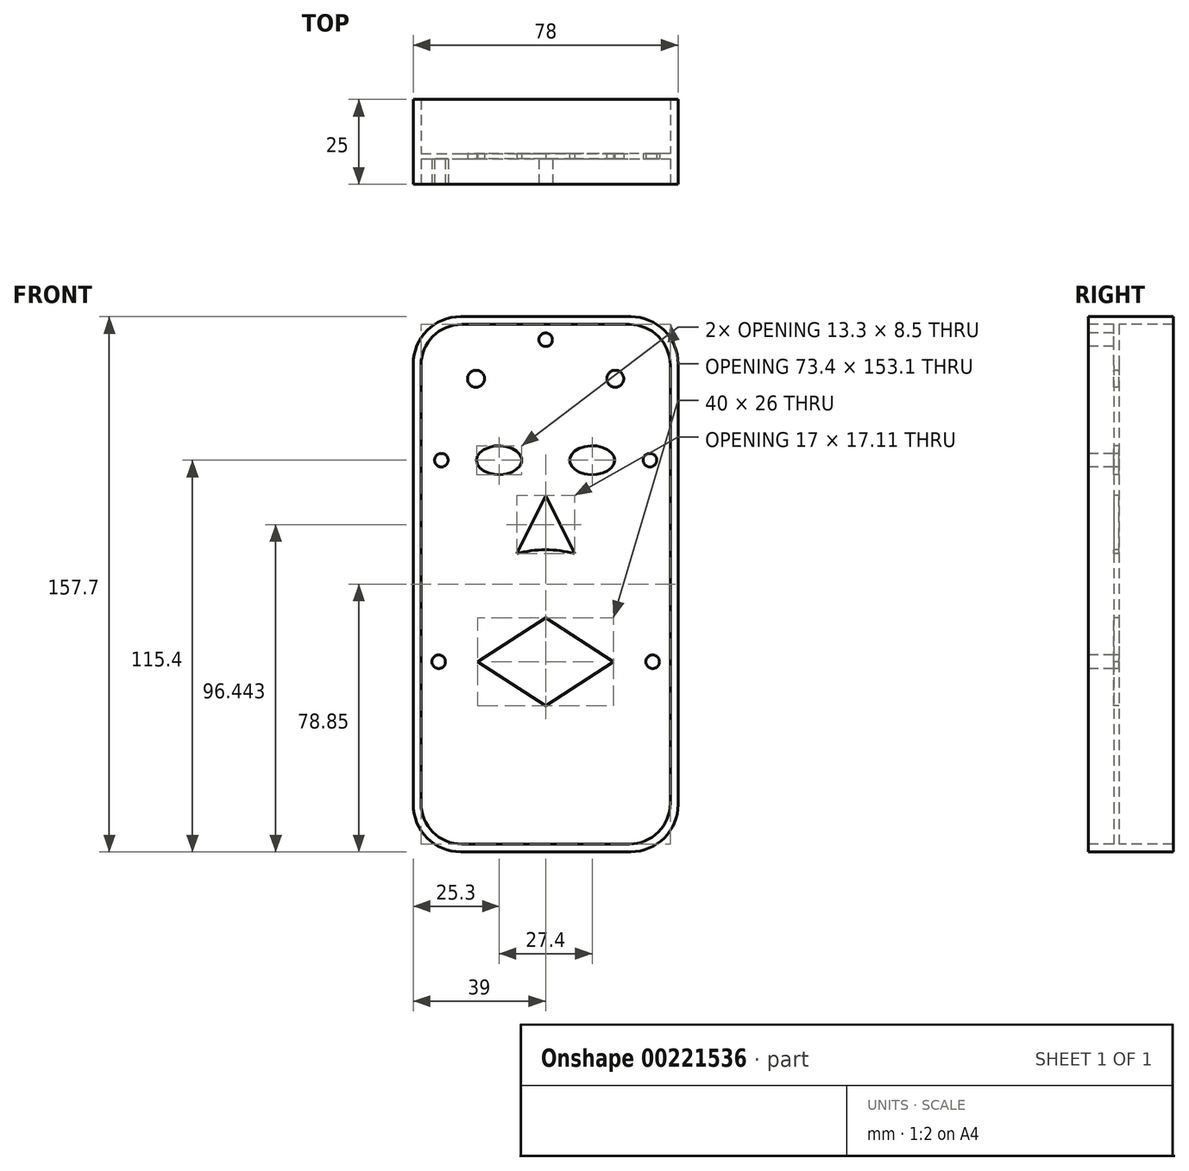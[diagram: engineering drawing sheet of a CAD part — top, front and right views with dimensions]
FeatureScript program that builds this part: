
annotation { "Feature Type Name" : "Feature", "Feature Type Description" : "" }
export const myFeature = defineFeature(function(context is Context, id is Id, definition is map)
    precondition{}
    {
        {
            var Q0;
            Q0=qCreatedBy(makeId("Front.planeOp"),FACE);
            var sketch = newSketch(context, id + "F0", { "sketchPlane" : qUnion([Q0])});
            skLineSegment(sketch, "E0.bottom", {"start": v(-39, 78.85) * mm, "end": v(39, 78.85) * mm});
            skLineSegment(sketch, "E0.top", {"start": v(-39, -78.85) * mm, "end": v(39, -78.85) * mm});
            skLineSegment(sketch, "E0.left", {"start": v(-39, 78.85) * mm, "end": v(-39, -78.85) * mm});
            skLineSegment(sketch, "E0.right", {"start": v(39, 78.85) * mm, "end": v(39, -78.85) * mm});
            skPoint(sketch, "E0.middle", {"position": v(0, 0) * mm});
            skLineSegment(sketch, "E1", {"start": v(-39, -22.85) * mm, "end": v(39, -22.85) * mm, "construction": true});
            skLineSegment(sketch, "E2", {"start": v(0, -9.85) * mm, "end": v(-20, -22.85) * mm});
            skPoint(sketch, "E2.startSnap0", {"position": v(0, -22.85) * mm});
            skLineSegment(sketch, "E3", {"start": v(-20, -22.85) * mm, "end": v(0, -35.85) * mm});
            skLineSegment(sketch, "E4.MirrorCS", {"start": v(0, -9.85) * mm, "end": v(20, -22.85) * mm});
            skLineSegment(sketch, "E5.MirrorCS", {"start": v(20, -22.85) * mm, "end": v(0, -35.85) * mm});
            skLineSegment(sketch, "E6.0", {"start": v(-36.7, 76.55) * mm, "end": v(-36.7, -76.55) * mm});
            skLineSegment(sketch, "E6.1", {"start": v(-36.7, 76.55) * mm, "end": v(36.7, 76.55) * mm});
            skLineSegment(sketch, "E6.2", {"start": v(36.7, 76.55) * mm, "end": v(36.7, -76.55) * mm});
            skLineSegment(sketch, "E6.3", {"start": v(-36.7, -76.55) * mm, "end": v(36.7, -76.55) * mm});
            skCircle(sketch, "E7", {"center": v(-31.5, -22.85) * mm, "radius": 2 * mm});
            skCircle(sketch, "E8.MirrorC", {"center": v(31.5, -22.85) * mm, "radius": 2 * mm});
            skArc(sketch, "E9", {"start": v(0, 10.15) * mm, "mid": v(-4.29, 9.87) * mm, "end": v(-8.5, 9.04) * mm});
            skLineSegment(sketch, "E10", {"start": v(-8.5, 9.04) * mm, "end": v(0, 26.15) * mm});
            skCircle(sketch, "E11", {"center": v(-3.04, 12.52) * mm, "radius": 2.5 * mm});
            skLineSegment(sketch, "E12.MirrorCS", {"start": v(8.5, 9.04) * mm, "end": v(0, 26.15) * mm});
            skCircle(sketch, "E13.MirrorC", {"center": v(3.04, 12.52) * mm, "radius": 2.5 * mm});
            skArc(sketch, "E14.MirrorCS", {"start": v(0, 10.15) * mm, "mid": v(4.29, 9.87) * mm, "end": v(8.5, 9.04) * mm});
            skLineSegment(sketch, "E15", {"start": v(-36.7, 36.55) * mm, "end": v(36.7, 36.55) * mm, "construction": true});
            skCircle(sketch, "E16", {"center": v(-30.7, 36.55) * mm, "radius": 2 * mm});
            skEllipse(sketch, "E17", {"center": v(-13.7, 36.55) * mm, "majorRadius": 6.65 * mm, "minorRadius": 4.25 * mm, "majorAxis": v(-1, 0)});
            skLineSegment(sketch, "E18", {"start": v(-36.7, 60.55) * mm, "end": v(36.7, 60.55) * mm, "construction": true});
            skCircle(sketch, "E19", {"center": v(0, 72.05) * mm, "radius": 2 * mm});
            skPoint(sketch, "E19.centerSnap0", {"position": v(0, 76.55) * mm});
            skCircle(sketch, "E20", {"center": v(-20.5, 60.55) * mm, "radius": 2.5 * mm});
            skCircle(sketch, "E21.MirrorC", {"center": v(20.5, 60.55) * mm, "radius": 2.5 * mm});
            skEllipse(sketch, "E22.MirrorC", {"center": v(13.7, 36.55) * mm, "majorRadius": 6.65 * mm, "minorRadius": 4.25 * mm, "majorAxis": v(1, 0)});
            skCircle(sketch, "E23.MirrorC", {"center": v(30.7, 36.55) * mm, "radius": 2 * mm});
            skCircle(sketch, "E24", {"center": v(-30.7, 36.55) * mm, "radius": 4.5 * mm, "construction": true});
            skPoint(sketch, "E25", {"position": v(0, 36.55) * mm});
            skArc(sketch, "E26", {"start": v(-2.86, 42.64) * mm, "mid": v(-2.2, 36.47) * mm, "end": v(-2.9, 30.3) * mm, "construction": true});
            skLineSegment(sketch, "E27", {"start": v(-30.7, 36.55) * mm, "end": v(-2.86, 42.64) * mm, "construction": true});
            skLineSegment(sketch, "E28", {"start": v(-30.7, 36.55) * mm, "end": v(-2.9, 30.3) * mm, "construction": true});
            skLineSegment(sketch, "E29", {"start": v(-2.86, 42.64) * mm, "end": v(-30.99, 38.53) * mm, "construction": true});
            skLineSegment(sketch, "E30", {"start": v(-2.9, 30.3) * mm, "end": v(-31, 34.57) * mm, "construction": true});
            skSolve(sketch);
        }
        {
            var Q0;
            {var subQ1=sQuery(id+"F0.wireOp",EDGE,"E10");Q0=makeQuery(id+"F0.imprint","IMPRINT",FACE,{"disambiguationData":[TD([[makeQuery(id+"F0.imprint","IMPRINT",EDGE,{"derivedFrom":subQ1}),-1.0]])]});}
            var Q1;
            Q1=makeQuery(id+"F0.imprint","IMPRINT",FACE,{"disambiguationData":[TD([[makeQuery(id+"F0.imprint","IMPRINT",EDGE,{"derivedFrom":sQuery(id+"F0.wireOp",EDGE,"E2")}),-1.0]])]});
            var Q2;
            Q2=makeQuery(id+"F0.imprint","IMPRINT",FACE,{"disambiguationData":[TD([[makeQuery(id+"F0.imprint","IMPRINT",EDGE,{"derivedFrom":sQuery(id+"F0.wireOp",EDGE,"E0.bottom")}),-1.0]])]});
            var Q3;
            Q3=makeQuery(id+"F0.imprint","IMPRINT",FACE,{"disambiguationData":[TD([[makeQuery(id+"F0.imprint","IMPRINT",EDGE,{"derivedFrom":sQuery(id+"F0.wireOp",EDGE,"E19")}),1.0]])]});
            var Q4;
            Q4=makeQuery(id+"F0.imprint","IMPRINT",FACE,{"disambiguationData":[TD([[makeQuery(id+"F0.imprint","IMPRINT",EDGE,{"derivedFrom":sQuery(id+"F0.wireOp",EDGE,"E23.MirrorC")}),-1.0]])]});
            var Q5;
            Q5=makeQuery(id+"F0.imprint","IMPRINT",FACE,{"disambiguationData":[TD([[makeQuery(id+"F0.imprint","IMPRINT",EDGE,{"derivedFrom":sQuery(id+"F0.wireOp",EDGE,"E16")}),1.0]])]});
            var Q6;
            Q6=makeQuery(id+"F0.imprint","IMPRINT",FACE,{"disambiguationData":[TD([[makeQuery(id+"F0.imprint","IMPRINT",EDGE,{"derivedFrom":sQuery(id+"F0.wireOp",EDGE,"E7")}),1.0]])]});
            var Q7;
            Q7=makeQuery(id+"F0.imprint","IMPRINT",FACE,{"disambiguationData":[TD([[makeQuery(id+"F0.imprint","IMPRINT",EDGE,{"derivedFrom":sQuery(id+"F0.wireOp",EDGE,"E8.MirrorC")}),-1.0]])]});
            var Q8;
            Q8=makeQuery(id+"F0.imprint","IMPRINT",FACE,{"disambiguationData":[TD([[makeQuery(id+"F0.imprint","IMPRINT",EDGE,{"derivedFrom":sQuery(id+"F0.wireOp",EDGE,"E20")}),1.0]])]});
            var Q9;
            Q9=makeQuery(id+"F0.imprint","IMPRINT",FACE,{"disambiguationData":[TD([[makeQuery(id+"F0.imprint","IMPRINT",EDGE,{"derivedFrom":sQuery(id+"F0.wireOp",EDGE,"E21.MirrorC")}),-1.0]])]});
            var Q10;
            Q10=makeQuery(id+"F0.imprint","IMPRINT",FACE,{"disambiguationData":[TD([[makeQuery(id+"F0.imprint","IMPRINT",EDGE,{"derivedFrom":sQuery(id+"F0.wireOp",EDGE,"E17")}),1.0]])]});
            var Q11;
            Q11=makeQuery(id+"F0.imprint","IMPRINT",FACE,{"disambiguationData":[TD([[makeQuery(id+"F0.imprint","IMPRINT",EDGE,{"derivedFrom":sQuery(id+"F0.wireOp",EDGE,"E22.MirrorC")}),1.0]])]});
            var Q12;
            Q12=makeQuery(id+"F0.imprint","IMPRINT",FACE,{"disambiguationData":[TD([[makeQuery(id+"F0.imprint","IMPRINT",EDGE,{"derivedFrom":sQuery(id+"F0.wireOp",EDGE,"E11")}),1.0]])]});
            var Q13;
            Q13=makeQuery(id+"F0.imprint","IMPRINT",FACE,{"disambiguationData":[TD([[makeQuery(id+"F0.imprint","IMPRINT",EDGE,{"derivedFrom":sQuery(id+"F0.wireOp",EDGE,"E13.MirrorC")}),-1.0]])]});
            var Q14;
            Q14=makeQuery(id+"F0.imprint","IMPRINT",FACE,{"disambiguationData":[TD([[makeQuery(id+"F0.imprint","IMPRINT",EDGE,{"derivedFrom":sQuery(id+"F0.wireOp",EDGE,"E2")}),1.0]])]});
            extrude(context, id + "F1", {"entities" : qUnion([Q0, Q1, Q2, Q3, Q4, Q5, Q6, Q7, Q8, Q9, Q10, Q11, Q12, Q13, Q14]), "oppositeDirection" : true, "depth" : 2.3 * mm});
        }
        {
            var Q0;
            Q0=makeQuery(id+"F0.imprint","IMPRINT",FACE,{"disambiguationData":[TD([[makeQuery(id+"F0.imprint","IMPRINT",EDGE,{"derivedFrom":sQuery(id+"F0.wireOp",EDGE,"E7")}),1.0]])]});
            var Q1;
            Q1=makeQuery(id+"F0.imprint","IMPRINT",FACE,{"disambiguationData":[TD([[makeQuery(id+"F0.imprint","IMPRINT",EDGE,{"derivedFrom":sQuery(id+"F0.wireOp",EDGE,"E8.MirrorC")}),-1.0]])]});
            var Q2;
            Q2=makeQuery(id+"F0.imprint","IMPRINT",FACE,{"disambiguationData":[TD([[makeQuery(id+"F0.imprint","IMPRINT",EDGE,{"derivedFrom":sQuery(id+"F0.wireOp",EDGE,"E16")}),1.0]])]});
            var Q3;
            Q3=makeQuery(id+"F0.imprint","IMPRINT",FACE,{"disambiguationData":[TD([[makeQuery(id+"F0.imprint","IMPRINT",EDGE,{"derivedFrom":sQuery(id+"F0.wireOp",EDGE,"E23.MirrorC")}),-1.0]])]});
            var Q4;
            Q4=makeQuery(id+"F0.imprint","IMPRINT",FACE,{"disambiguationData":[TD([[makeQuery(id+"F0.imprint","IMPRINT",EDGE,{"derivedFrom":sQuery(id+"F0.wireOp",EDGE,"E19")}),1.0]])]});
            extrude(context, id + "F2", {"entities" : qUnion([Q0, Q1, Q2, Q3, Q4]), "operationType" : NewBodyOperationType.ADD, "oppositeDirection" : true, "depth" : 9 * mm});
        }
        {
            var Q0;
            Q0=makeQuery(id+"F0.imprint","IMPRINT",FACE,{"disambiguationData":[TD([[makeQuery(id+"F0.imprint","IMPRINT",EDGE,{"derivedFrom":sQuery(id+"F0.wireOp",EDGE,"E11")}),1.0]])]});
            var Q1;
            Q1=makeQuery(id+"F0.imprint","IMPRINT",FACE,{"disambiguationData":[TD([[makeQuery(id+"F0.imprint","IMPRINT",EDGE,{"derivedFrom":sQuery(id+"F0.wireOp",EDGE,"E13.MirrorC")}),-1.0]])]});
            var Q2;
            Q2=makeQuery(id+"F0.imprint","IMPRINT",FACE,{"disambiguationData":[TD([[makeQuery(id+"F0.imprint","IMPRINT",EDGE,{"derivedFrom":sQuery(id+"F0.wireOp",EDGE,"E20")}),1.0]])]});
            var Q3;
            Q3=makeQuery(id+"F0.imprint","IMPRINT",FACE,{"disambiguationData":[TD([[makeQuery(id+"F0.imprint","IMPRINT",EDGE,{"derivedFrom":sQuery(id+"F0.wireOp",EDGE,"E21.MirrorC")}),-1.0]])]});
            var Q4;
            Q4=makeQuery(id+"F0.imprint","IMPRINT",FACE,{"disambiguationData":[TD([[makeQuery(id+"F0.imprint","IMPRINT",EDGE,{"derivedFrom":sQuery(id+"F0.wireOp",EDGE,"E17")}),1.0]])]});
            var Q5;
            Q5=makeQuery(id+"F0.imprint","IMPRINT",FACE,{"disambiguationData":[TD([[makeQuery(id+"F0.imprint","IMPRINT",EDGE,{"derivedFrom":sQuery(id+"F0.wireOp",EDGE,"E22.MirrorC")}),1.0]])]});
            var Q6;
            Q6=makeQuery(id+"F0.imprint","IMPRINT",FACE,{"disambiguationData":[TD([[makeQuery(id+"F0.imprint","IMPRINT",EDGE,{"derivedFrom":sQuery(id+"F0.wireOp",EDGE,"E2")}),1.0]])]});
            extrude(context, id + "F3", {"entities" : qUnion([Q0, Q1, Q2, Q3, Q4, Q5, Q6]), "operationType" : NewBodyOperationType.REMOVE, "endBound" : BoundingType.SYMMETRIC, "oppositeDirection" : true, "depth" : 15 * mm});
        }
        {
            var Q0;
            Q0=makeQuery(id+"F0.imprint","IMPRINT",FACE,{"disambiguationData":[TD([[makeQuery(id+"F0.imprint","IMPRINT",EDGE,{"derivedFrom":sQuery(id+"F0.wireOp",EDGE,"E0.bottom")}),-1.0]])]});
            extrude(context, id + "F4", {"entities" : qUnion([Q0]), "operationType" : NewBodyOperationType.ADD, "oppositeDirection" : true, "depth" : 25 * mm});
        }
        {
            var Q0;
            Q0=makeQuery(id+"F4.opExtrude","SWEPT_EDGE",EDGE,{"disambiguationData":[OSD([sQuery(id+"F0.wireOp",EDGE,"E6.1"),sQuery(id+"F0.wireOp",EDGE,"E6.2")])]});
            var Q1;
            Q1=makeQuery(id+"F4.opExtrude","SWEPT_EDGE",EDGE,{"disambiguationData":[OSD([sQuery(id+"F0.wireOp",EDGE,"E6.0"),sQuery(id+"F0.wireOp",EDGE,"E6.1")])]});
            var Q2;
            Q2=makeQuery(id+"F4.opExtrude","SWEPT_EDGE",EDGE,{"disambiguationData":[OSD([sQuery(id+"F0.wireOp",EDGE,"E6.2"),sQuery(id+"F0.wireOp",EDGE,"E6.3")])]});
            var Q3;
            Q3=makeQuery(id+"F4.opExtrude","SWEPT_EDGE",EDGE,{"disambiguationData":[OSD([sQuery(id+"F0.wireOp",EDGE,"E6.0"),sQuery(id+"F0.wireOp",EDGE,"E6.3")])]});
            fillet(context, id + "F5", {"entities" : qUnion([Q0, Q1, Q2, Q3]), "radius" : 12 * mm, "tangentPropagation" : true, "allowEdgeOverflow" : false});
        }
        {
            var Q0;
            {var subQ0=sQuery(id+"F0.wireOp",EDGE,"E0.right");var subQ1=sQuery(id+"F0.wireOp",EDGE,"E0.top");Q0=makeQuery(id+"F4.boolean.opBoolean","MERGE",EDGE,{"derivedFrom":[makeQuery(id+"F1.opExtrude","SWEPT_EDGE",EDGE,{"disambiguationData":[OSD([subQ1,subQ0])]}),makeQuery(id+"F4.opExtrude","SWEPT_EDGE",EDGE,{"disambiguationData":[OSD([subQ1,subQ0])]})]});}
            var Q1;
            {var subQ0=sQuery(id+"F0.wireOp",EDGE,"E0.left");var subQ1=sQuery(id+"F0.wireOp",EDGE,"E0.top");Q1=makeQuery(id+"F4.boolean.opBoolean","MERGE",EDGE,{"derivedFrom":[makeQuery(id+"F1.opExtrude","SWEPT_EDGE",EDGE,{"disambiguationData":[OSD([subQ1,subQ0])]}),makeQuery(id+"F4.opExtrude","SWEPT_EDGE",EDGE,{"disambiguationData":[OSD([subQ1,subQ0])]})]});}
            var Q2;
            {var subQ0=sQuery(id+"F0.wireOp",EDGE,"E0.left");var subQ1=sQuery(id+"F0.wireOp",EDGE,"E0.bottom");Q2=makeQuery(id+"F4.boolean.opBoolean","MERGE",EDGE,{"derivedFrom":[makeQuery(id+"F1.opExtrude","SWEPT_EDGE",EDGE,{"disambiguationData":[OSD([subQ1,subQ0])]}),makeQuery(id+"F4.opExtrude","SWEPT_EDGE",EDGE,{"disambiguationData":[OSD([subQ1,subQ0])]})]});}
            var Q3;
            {var subQ0=sQuery(id+"F0.wireOp",EDGE,"E0.right");var subQ1=sQuery(id+"F0.wireOp",EDGE,"E0.bottom");Q3=makeQuery(id+"F4.boolean.opBoolean","MERGE",EDGE,{"derivedFrom":[makeQuery(id+"F1.opExtrude","SWEPT_EDGE",EDGE,{"disambiguationData":[OSD([subQ1,subQ0])]}),makeQuery(id+"F4.opExtrude","SWEPT_EDGE",EDGE,{"disambiguationData":[OSD([subQ1,subQ0])]})]});}
            fillet(context, id + "F6", {"entities" : qUnion([Q0, Q1, Q2, Q3]), "radius" : 14 * mm, "tangentPropagation" : true, "allowEdgeOverflow" : false});
        }
    });
